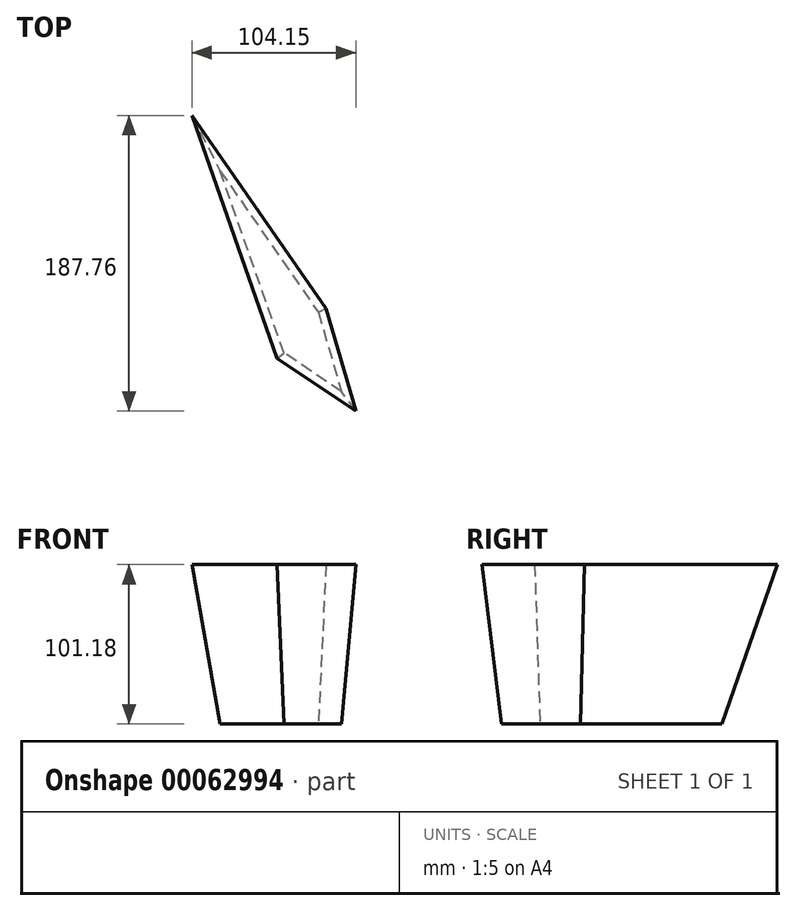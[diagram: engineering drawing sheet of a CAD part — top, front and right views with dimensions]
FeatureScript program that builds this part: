
annotation { "Feature Type Name" : "Feature", "Feature Type Description" : "" }
export const myFeature = defineFeature(function(context is Context, id is Id, definition is map)
    precondition{}
    {
        {
            var Q0;
            Q0=qCreatedBy(makeId("Top.planeOp"),FACE);
            var sketch = newSketch(context, id + "F0", { "sketchPlane" : qUnion([Q0])});
            skLineSegment(sketch, "E0", {"start": v(-44.89, -36.05) * mm, "end": v(-8.44, -60.44) * mm});
            skLineSegment(sketch, "E1", {"start": v(-8.44, -60.44) * mm, "end": v(-23.12, -10.2) * mm});
            skLineSegment(sketch, "E2", {"start": v(-23.12, -10.2) * mm, "end": v(-85.46, 79.62) * mm});
            skLineSegment(sketch, "E3", {"start": v(-85.46, 79.62) * mm, "end": v(-44.89, -36.05) * mm});
            skSolve(sketch);
        }
        {
            var Q0;
            Q0=makeQuery(id+"F0.imprint","IMPRINT",FACE,{"disambiguationData":[TD([[makeQuery(id+"F0.imprint","IMPRINT",EDGE,{"derivedFrom":sQuery(id+"F0.wireOp",EDGE,"E0")}),1.0]])]});
            extrude(context, id + "F1", {"entities" : qUnion([Q0]), "depth" : 101.18 * mm, "hasDraft" : true, "draftAngle" : 3 * degree});
        }
    });
